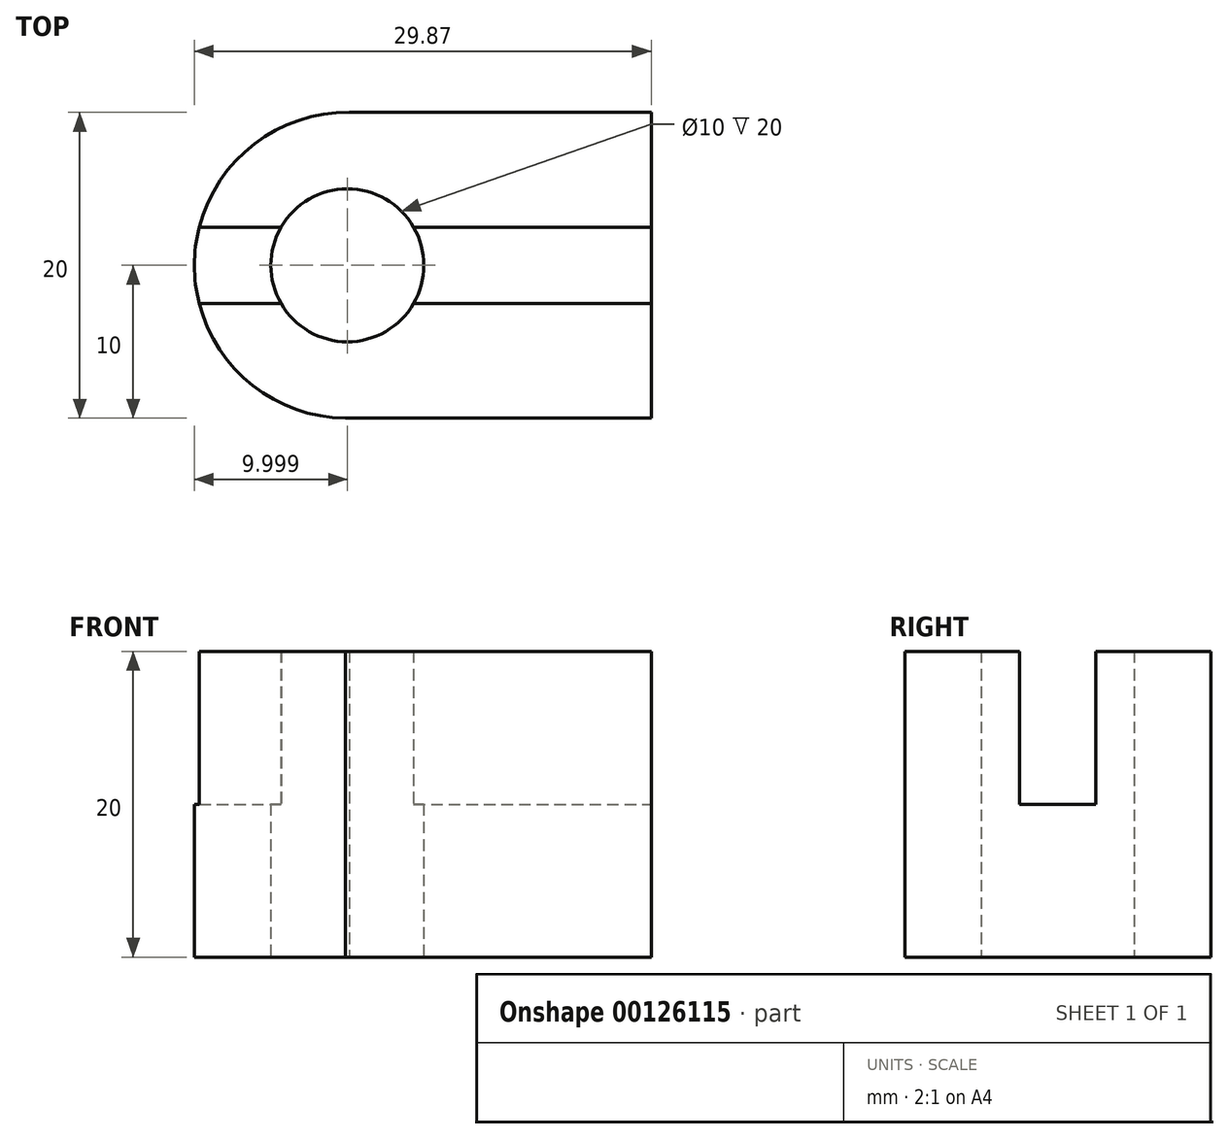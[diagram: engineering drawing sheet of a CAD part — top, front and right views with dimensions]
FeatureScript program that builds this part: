
annotation { "Feature Type Name" : "Feature", "Feature Type Description" : "" }
export const myFeature = defineFeature(function(context is Context, id is Id, definition is map)
    precondition{}
    {
        {
            var Q0;
            Q0=qCreatedBy(makeId("Top.planeOp"),FACE);
            var sketch = newSketch(context, id + "F0", { "sketchPlane" : qUnion([Q0])});
            skCircle(sketch, "E0", {"center": v(-34.81, 0) * mm, "radius": 10 * mm});
            skLineSegment(sketch, "E1.bottom", {"start": v(-34.94, 10) * mm, "end": v(-14.94, 10) * mm});
            skLineSegment(sketch, "E1.top", {"start": v(-34.94, -10) * mm, "end": v(-14.94, -10) * mm});
            skLineSegment(sketch, "E1.left", {"start": v(-34.94, 10) * mm, "end": v(-34.94, -10) * mm});
            skLineSegment(sketch, "E1.right", {"start": v(-14.94, 10) * mm, "end": v(-14.94, -10) * mm});
            skCircle(sketch, "E2", {"center": v(-34.81, 0) * mm, "radius": 5 * mm});
            skSolve(sketch);
        }
        {
            var Q0;
            Q0 = qSketchRegion(id + "F0", true);
            extrude(context, id + "F1", {"entities" : qUnion([Q0]), "depth" : 20 * mm});
        }
        {
            var Q0;
            Q0=makeQuery(id+"F1.opExtrude","SWEPT_FACE",FACE,{"disambiguationData":[OSD([sQuery(id+"F0.wireOp",EDGE,"E1.right")])]});
            var sketch = newSketch(context, id + "F2", { "sketchPlane" : qUnion([Q0])});
            skLineSegment(sketch, "E3.bottom", {"start": v(-2.5, 20) * mm, "end": v(2.5, 20) * mm});
            skLineSegment(sketch, "E3.top", {"start": v(-2.5, 10) * mm, "end": v(2.5, 10) * mm});
            skLineSegment(sketch, "E3.left", {"start": v(-2.5, 20) * mm, "end": v(-2.5, 10) * mm});
            skLineSegment(sketch, "E3.right", {"start": v(2.5, 20) * mm, "end": v(2.5, 10) * mm});
            skSolve(sketch);
        }
        {
            var Q0;
            Q0 = qSketchRegion(id + "F2", true);
            extrude(context, id + "F3", {"entities" : qUnion([Q0]), "operationType" : NewBodyOperationType.REMOVE, "endBound" : BoundingType.THROUGH_ALL, "oppositeDirection" : true, "depth" : 25.4 * mm});
        }
    });
